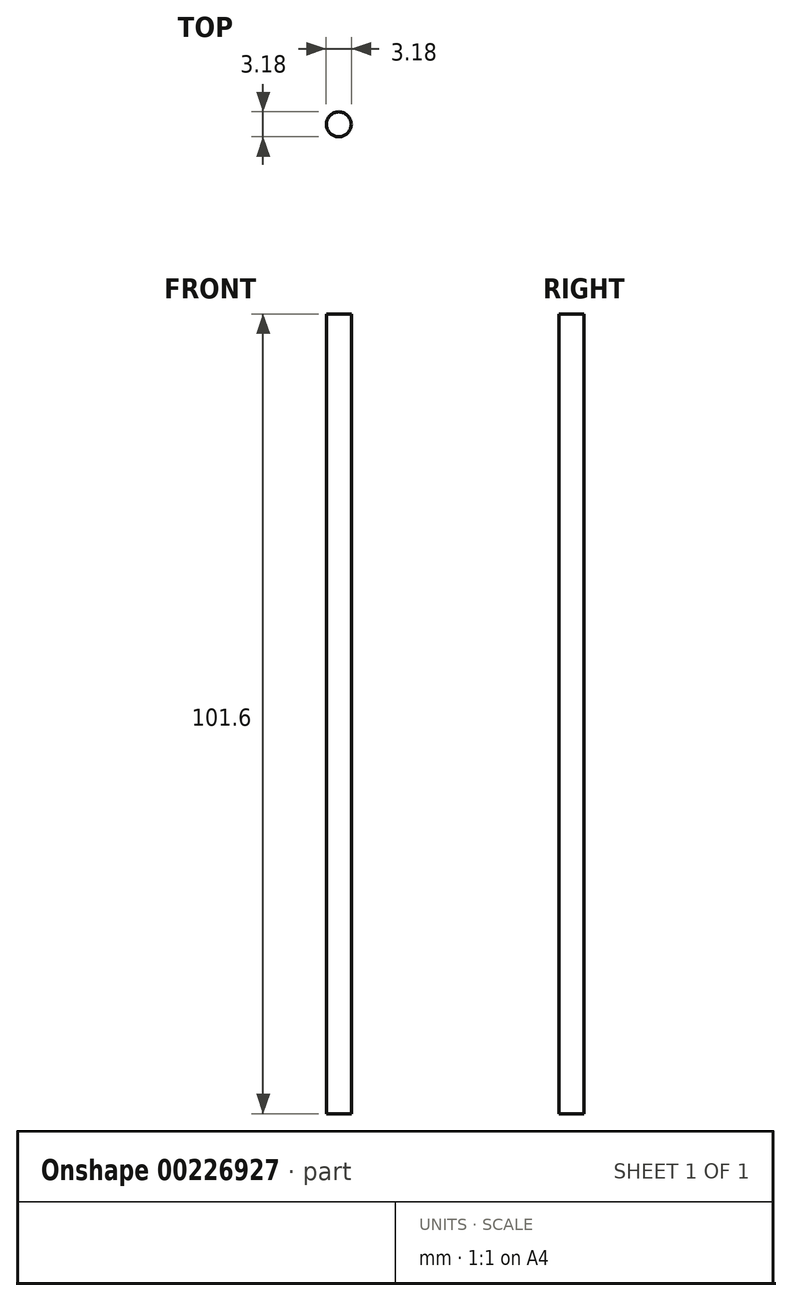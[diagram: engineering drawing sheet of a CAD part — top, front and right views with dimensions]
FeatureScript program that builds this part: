
annotation { "Feature Type Name" : "Feature", "Feature Type Description" : "" }
export const myFeature = defineFeature(function(context is Context, id is Id, definition is map)
    precondition{}
    {
        {
            var Q0;
            Q0=qCreatedBy(makeId("Top.planeOp"),FACE);
            var sketch = newSketch(context, id + "F0", { "sketchPlane" : qUnion([Q0])});
            skCircle(sketch, "E0", {"center": v(-54.05, 52.49) * mm, "radius": 1.59 * mm});
            skSolve(sketch);
        }
        {
            var Q0;
            Q0=makeQuery(id+"F0.imprint","IMPRINT",FACE,{"disambiguationData":[TD([[makeQuery(id+"F0.imprint","IMPRINT",EDGE,{"derivedFrom":sQuery(id+"F0.wireOp",EDGE,"E0")}),1.0]])]});
            extrude(context, id + "F1", {"entities" : qUnion([Q0]), "depth" : 101.6 * mm});
        }
    });
